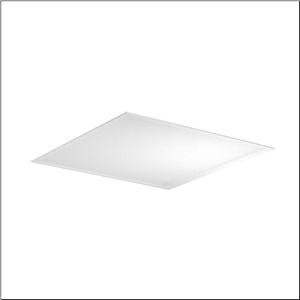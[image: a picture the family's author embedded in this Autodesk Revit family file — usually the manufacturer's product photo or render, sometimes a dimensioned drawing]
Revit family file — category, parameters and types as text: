
# Revit family: apollon_r__21_square_51mq12w72414_a86f
name_source: partatom
category: Lighting Fixtures
units: mm (PartAtom-declared; Revit-internal decimal feet)

## family parameters
Cut with Voids When Loaded = No
Host = Face
Light Source = No
Part Type = Normal
Room Calculation Point = No
Round Connector Dimension = Use Diameter
Shared = No

## types (1)
- Apollon® 21 square (1 x LED, 4200 lm, 23.3 W, 4000K)
    Apparent Load = 23 VA
    CIE Flux Codes = 60 87 97 100 100
    Color Rendering = 80
    Color Temperature = 4000K
    Default Elevation = 1800 mm
    Description = Apollon® 21 square, office luminaire, primary optical cover: micro prismatic cover, of PMMA, CAT 2 (L<= 3000cd/m²), light emission: direct distribution, primary light characteristic: symmetric, installation type: lay-in mounting, LED, rated luminous flux: 4.200lm, luminous efficacy: 180lm/W, light colour: 840, colour temperature: 4000K, with terminal, 3-pole, mains connection: 220..240V, AC/DC, 0/50..60Hz, rated input power: 23W, housing, of aluminium, coated, traffic white (RAL 9016), module: M600, length: 595mm, width: 595mm, height: 30mm, housing upper side, of sheet steel, galvanised, protection rating (complete): IP20, protection rating (lamp compartment, on room side): IP50, insulation class (complete): insulation class II (safety insulation), certification: CE, ENEC, impact resistance: IK03, permissible operating ambient temperature: -20..+45°C, permissible storage temperature: -40..+80°C, packaging unit: 1 piece
    Height = 0 mm  [stored 0 ft]
    Lamp = 1 x LED
    Lamp Light Flux = 4200 lm
    Lamp Power = 23.3 W
    Lamp count = 1
    Length = 595 mm
    Luminous efficacy = 180 lm/W
    Manufacturer = Siteco
    ModVariant = No
    Model = 51MQ12W72414
    Mounting Place = Ceiling
    Mounting Type = Recessed
    Number of Poles = 1
    OnlyDefault = Yes
    Power Factor = 1
    Product Name = Apollon® 21 square
    Product group = office luminaire | ceiling recessed
    ProductGroupID = 401
    Protection Class = Protection class II
    Protection Degree = IP 20
    RLX_Detail_Level = 1
    RLX_Emergency_Light_Flux = 0 lm
    RLX_Emergency_Type = 0
    RLX_Emergency_Type_DB = No
    RlxData = <blob elided: 12485 chars, md5=871fbcb6>
    Socket = socket
    Standby Power = 0 W
    System Light Flux = 4200 lm
    System Power = 23 W
    Type Comments = Product without accessories
    Type Image = l_1291049.jpg
    URL = http://relux.com
    VarID = ---
    Voltage = 0 V
    Weight = 0.00 kg
    Width = 595 mm

note: [stored X ft] marks values corroborated as IEEE doubles in the binary element streams (Revit-internal decimal feet)

## geometry (parser evidence)
native form markers: Sweep x11
no freeform markers — native parametric forms only
